# Revit family: flat_polymero_311945_002_1_2689
name_source: partatom
category: Lighting Fixtures
units: mm (PartAtom-declared; Revit-internal decimal feet)

## family parameters
Cut with Voids When Loaded = No
Host = Face
Light Source = No
Part Type = Normal
Room Calculation Point = No
Round Connector Dimension = Use Diameter
Shared = No

## types (1)
- FLAT POLYMERO (1 x LED Modul 830, 1150 lm, 3000)
    Apparent Load = 12 VA
    CIE Flux Codes = 43 73 91 89 100
    Color Rendering = 80
    Color Temperature = 3000
    Default Elevation = 1800 mm
    Description = Series: FLAT POLYMERO
Decorative round surface-mounted luminaire. Base: metal, powder-coated. Diffuser made of non-yellowing plastic (PMMA), opal. Diffuser fastening: patented push system. Suitable for Ceiling mounting, Wall (surface). 
Colour: white
Diameter: 360 mm
Height: 100 mm
Lamp: LED exchangeable
Socket: without socket
Colour temperature: 3000K
Colour rendering index (CRI): 83
System power: 12 W
Rated luminous flux: 1150 lm
Beam angle Down: 115°
Luminous efficiency: 96 lm/W
Control gear: AC Strom, dim.Ph.an-/abschnitt
Protection class: I
Type of protection: IP 40
    Height = 100 mm  [stored 0.328084 ft]
    Lamp = 1 x LED Modul 830
    Lamp Light Flux = 1150 lm
    Lamp count = 1
    Length = 360 mm
    Lifetime = 50000 h
    Luminous efficacy = 96 lm/W
    Manufacturer = RZB
    ModVariant = No
    Model = 311945.002.1
    Mounting Place = Ceiling, Wall
    Mounting Type = Surface mounted
    Number of Poles = 1
    OnlyDefault = Yes
    Power Factor = 1
    Product Name = FLAT POLYMERO
    Product group = Surface mounted ceiling and wall luminaires
    ProductGroupID = 305
    Protection Class = Protection class I
    Protection Degree = IP 40
    RLX_Detail_Level = 1
    RLX_Emergency_Light_Flux = 0 lm
    RLX_Emergency_Type = 0
    RLX_Emergency_Type_DB = No
    RlxData = <blob elided: 77269 chars, md5=6fd32fad>
    Socket = socket
    Standby Power = 0 W
    System Light Flux = 1150 lm
    System Power = 12 W
    Type Comments = ALEA SPOT
    Type Image = 311523.002.1.jpg
    URL = http://relux.com
    VarID = ---
    Voltage = 230 V
    Voltage Range = 220-240 V
    Weight = 0.00 kg
    Width = 0 mm  [stored 0 ft]

note: [stored X ft] marks values corroborated as IEEE doubles in the binary element streams (Revit-internal decimal feet)

## geometry (parser evidence)
native form markers: Sweep x12
no freeform markers — native parametric forms only
